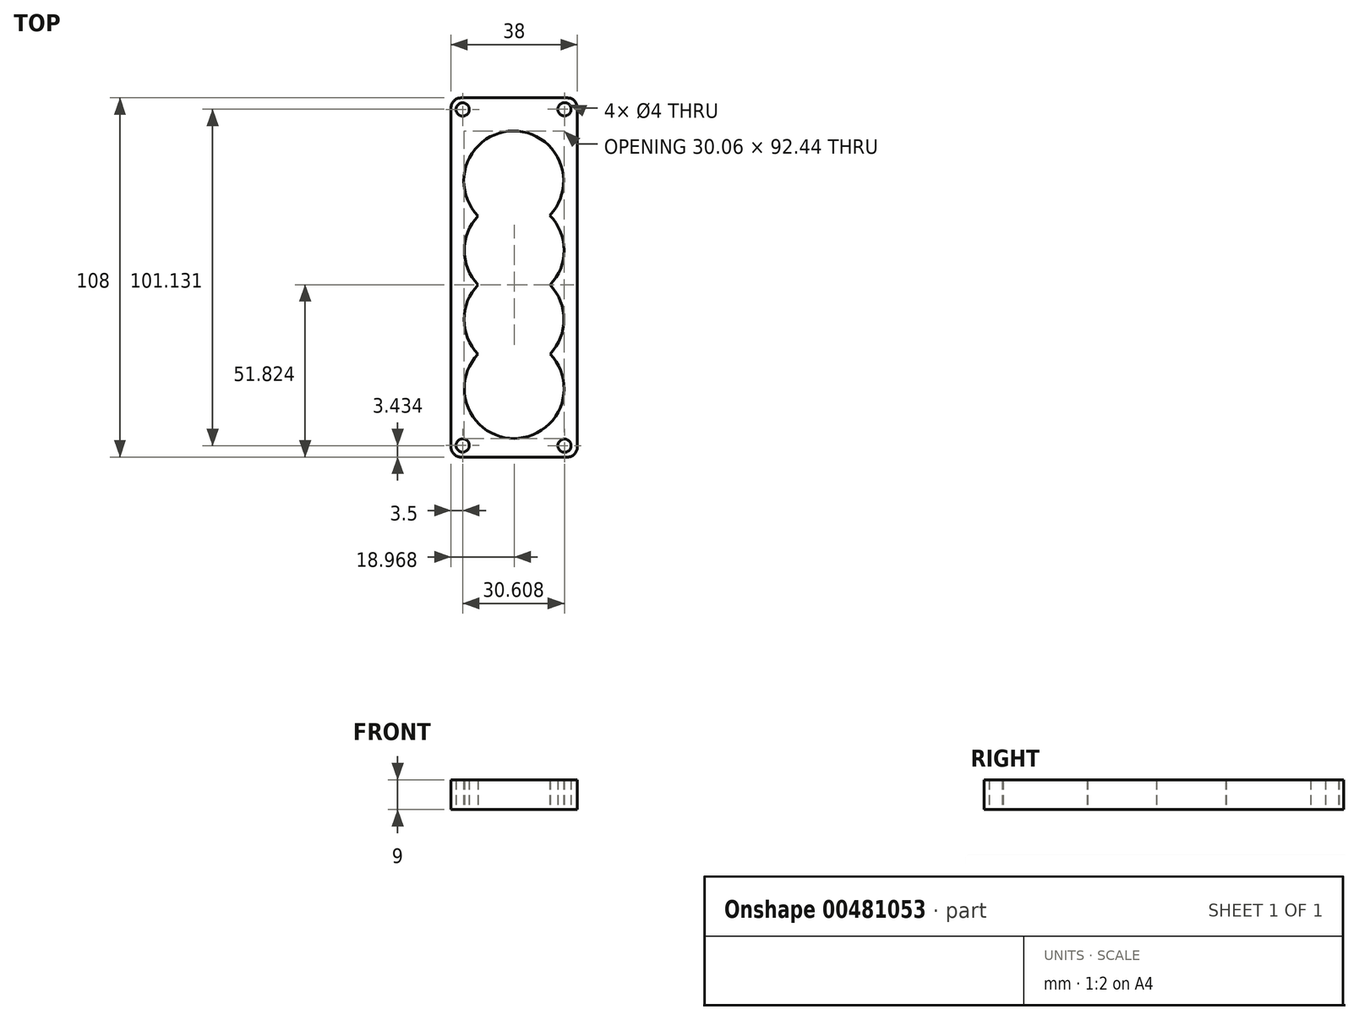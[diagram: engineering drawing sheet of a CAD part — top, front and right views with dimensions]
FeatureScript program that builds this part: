
annotation { "Feature Type Name" : "Feature", "Feature Type Description" : "" }
export const myFeature = defineFeature(function(context is Context, id is Id, definition is map)
    precondition{}
    {
        {
            var Q0;
            Q0=qCreatedBy(makeId("Top.planeOp"),FACE);
            var sketch = newSketch(context, id + "F0", { "sketchPlane" : qUnion([Q0])});
            skLineSegment(sketch, "E0", {"start": v(-0.18, 42.76) * mm, "end": v(0, -38.86) * mm, "construction": true});
            skCircle(sketch, "E1", {"center": v(-0.06, -12.62) * mm, "radius": 9 * mm});
            skCircle(sketch, "E2", {"center": v(-0.1, 8.22) * mm, "radius": 9 * mm});
            skCircle(sketch, "E3", {"center": v(-0.15, 29.04) * mm, "radius": 9 * mm});
            skPoint(sketch, "E4.oppositeSnap0", {"position": v(8.9, -24.62) * mm});
            skPoint(sketch, "E5.endSnap0", {"position": v(-13.1, -24.62) * mm});
            skCircle(sketch, "E6", {"center": v(10.35, 29.04) * mm, "radius": 1.25 * mm});
            skCircle(sketch, "E7", {"center": v(10.35, 8.22) * mm, "radius": 1.25 * mm});
            skCircle(sketch, "E8", {"center": v(10.35, -12.62) * mm, "radius": 1.25 * mm});
            skCircle(sketch, "E9.MirrorC", {"center": v(-10.65, 29) * mm, "radius": 1.25 * mm});
            skCircle(sketch, "E10.MirrorC", {"center": v(-10.56, 8.18) * mm, "radius": 1.25 * mm});
            skCircle(sketch, "E11.MirrorC", {"center": v(-10.47, -12.67) * mm, "radius": 1.25 * mm});
            skCircle(sketch, "E12", {"center": v(10.35, -33.38) * mm, "radius": 1.25 * mm});
            skCircle(sketch, "E13", {"center": v(-10.47, -33.43) * mm, "radius": 1.25 * mm});
            skCircle(sketch, "E14", {"center": v(-0.02, -33.4) * mm, "radius": 9 * mm});
            skLineSegment(sketch, "E15", {"start": v(-0.1, 8.22) * mm, "end": v(-23.14, 8.17) * mm, "construction": true});
            skLineSegment(sketch, "E16", {"start": v(-0.06, -12.62) * mm, "end": v(-20.8, -12.67) * mm, "construction": true});
            skLineSegment(sketch, "E17", {"start": v(12.8, -12.1) * mm, "end": v(12.8, -12.85) * mm});
            skLineSegment(sketch, "E18", {"start": v(-13.03, -12.27) * mm, "end": v(-13.03, -12.78) * mm});
            skLineSegment(sketch, "E19", {"start": v(-13.37, 8.31) * mm, "end": v(-13.37, 8.08) * mm});
            skLineSegment(sketch, "E20", {"start": v(13.19, 8.34) * mm, "end": v(13.19, 8.17) * mm});
            skCircle(sketch, "E21", {"center": v(-10.47, -12.67) * mm, "radius": 2.25 * mm});
            skCircle(sketch, "E22", {"center": v(10.35, -12.62) * mm, "radius": 2.25 * mm});
            skPoint(sketch, "E23.startSnap0", {"position": v(-9, -2.31) * mm});
            skPoint(sketch, "E23.endSnap0", {"position": v(-9.76, -22) * mm});
            skPoint(sketch, "E24.startSnap0", {"position": v(-9.04, 18.63) * mm});
            skCircle(sketch, "E25", {"center": v(-0.15, 29.04) * mm, "radius": 15 * mm});
            skCircle(sketch, "E26", {"center": v(-0.02, -33.4) * mm, "radius": 15 * mm});
            skCircle(sketch, "E27", {"center": v(-10.56, 8.18) * mm, "radius": 2.5 * mm});
            skCircle(sketch, "E28", {"center": v(10.35, 8.22) * mm, "radius": 2.5 * mm});
            skCircle(sketch, "E29", {"center": v(10.35, 29.04) * mm, "radius": 2.5 * mm});
            skCircle(sketch, "E30", {"center": v(-10.65, 29) * mm, "radius": 2.5 * mm});
            skCircle(sketch, "E31", {"center": v(-10.47, -33.43) * mm, "radius": 2.5 * mm});
            skCircle(sketch, "E32", {"center": v(10.35, -33.38) * mm, "radius": 2.5 * mm});
            skCircle(sketch, "E33", {"center": v(-0.06, -12.62) * mm, "radius": 15 * mm});
            skCircle(sketch, "E34", {"center": v(0, 8.16) * mm, "radius": 15 * mm});
            skLineSegment(sketch, "E35.bottom", {"start": v(-19, 54) * mm, "end": v(19, 54) * mm});
            skLineSegment(sketch, "E35.top", {"start": v(-19, -54) * mm, "end": v(19, -54) * mm});
            skLineSegment(sketch, "E35.left", {"start": v(-19, 54) * mm, "end": v(-19, -54) * mm});
            skLineSegment(sketch, "E35.right", {"start": v(19, 54) * mm, "end": v(19, -54) * mm});
            skCircle(sketch, "E36", {"center": v(-15.5, 50.5) * mm, "radius": 2 * mm});
            skCircle(sketch, "E37.MirrorC", {"center": v(-15.5, -50.5) * mm, "radius": 2 * mm});
            skCircle(sketch, "E38.MirrorC", {"center": v(15.1, 50.57) * mm, "radius": 2 * mm});
            skCircle(sketch, "E39.MirrorC", {"center": v(15.1, -50.57) * mm, "radius": 2 * mm});
            skSolve(sketch);
        }
        {
            var Q0;
            Q0=qSketchRegion(id+"F0",true);
            extrude(context, id + "F1", {"entities" : qUnion([Q0]), "depth" : 9 * mm});
        }
        {
            var Q0;
            Q0=makeQuery(id+"F1.opExtrude","SWEPT_EDGE",EDGE,{"disambiguationData":[OSD([sQuery(id+"F0.wireOp",EDGE,"E35.bottom"),sQuery(id+"F0.wireOp",EDGE,"E35.right")])]});
            var Q1;
            Q1=makeQuery(id+"F1.opExtrude","SWEPT_EDGE",EDGE,{"disambiguationData":[OSD([sQuery(id+"F0.wireOp",EDGE,"E35.top"),sQuery(id+"F0.wireOp",EDGE,"E35.right")])]});
            var Q2;
            Q2=makeQuery(id+"F1.opExtrude","SWEPT_EDGE",EDGE,{"disambiguationData":[OSD([sQuery(id+"F0.wireOp",EDGE,"E35.top"),sQuery(id+"F0.wireOp",EDGE,"E35.left")])]});
            var Q3;
            Q3=makeQuery(id+"F1.opExtrude","SWEPT_EDGE",EDGE,{"disambiguationData":[OSD([sQuery(id+"F0.wireOp",EDGE,"E35.bottom"),sQuery(id+"F0.wireOp",EDGE,"E35.left")])]});
            fillet(context, id + "F2", {"entities" : qUnion([Q0, Q1, Q2, Q3]), "radius" : 3 * mm, "tangentPropagation" : true, "allowEdgeOverflow" : false});
        }
    });
